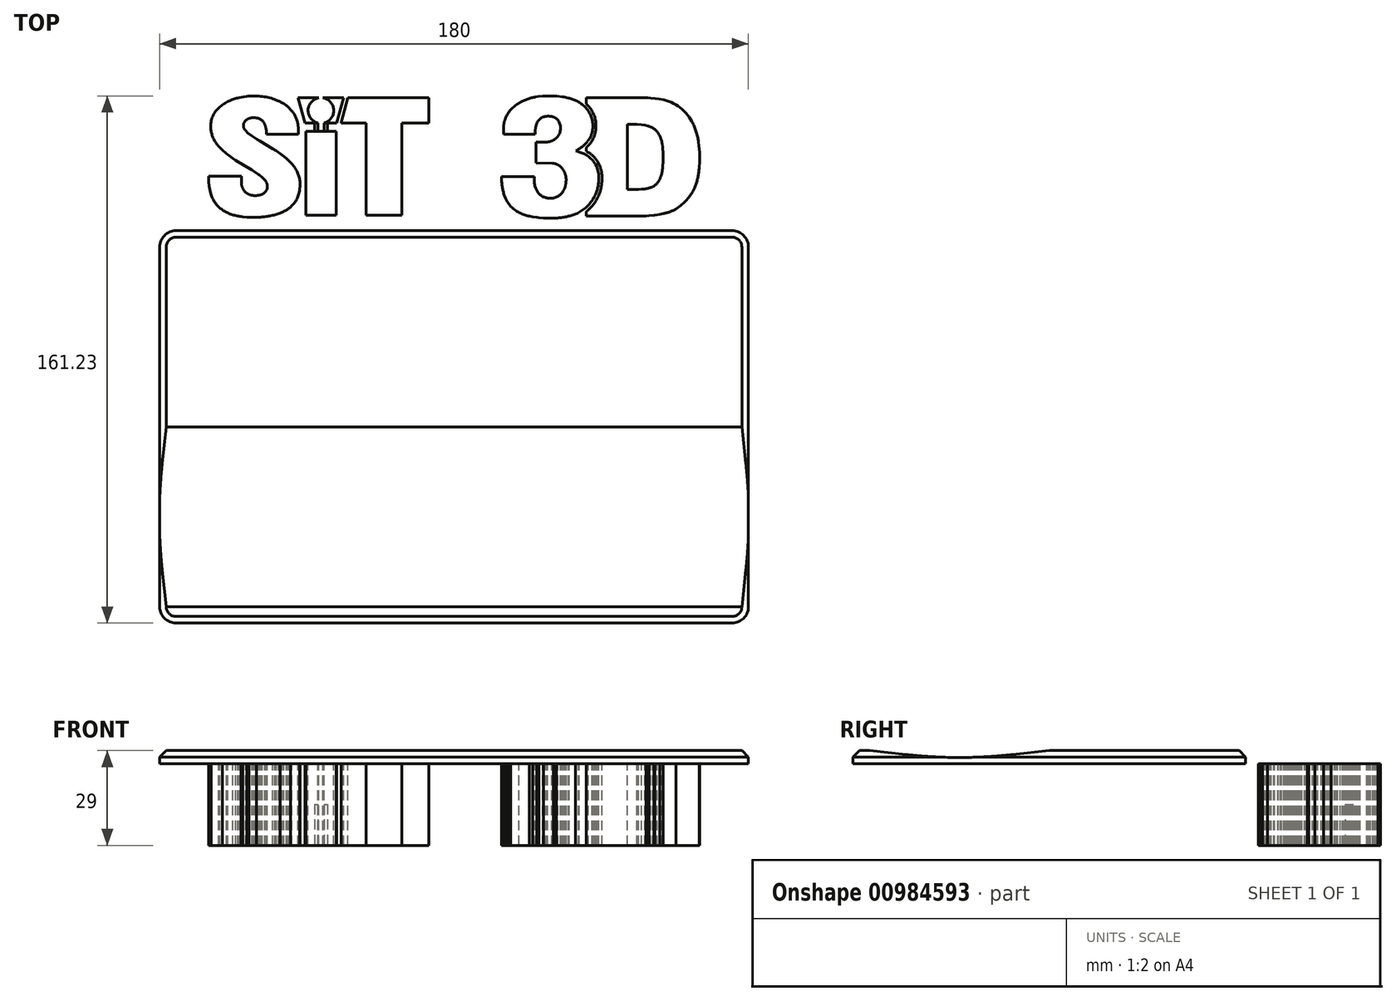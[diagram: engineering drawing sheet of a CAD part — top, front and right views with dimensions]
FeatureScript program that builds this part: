
annotation { "Feature Type Name" : "Feature", "Feature Type Description" : "" }
export const myFeature = defineFeature(function(context is Context, id is Id, definition is map)
    precondition{}
    {
        {
            var Q0;
            Q0=qCreatedBy(makeId("Top.planeOp"),FACE);
            var sketch = newSketch(context, id + "F0", { "sketchPlane" : qUnion([Q0])});
            skLineSegment(sketch, "E0", {"start": v(-41.68, 10.42) * mm, "end": v(-45.54, 10.42) * mm});
            skLineSegment(sketch, "E1", {"start": v(-45.54, 10.42) * mm, "end": v(-47.67, 18.07) * mm});
            skLineSegment(sketch, "E2", {"start": v(-47.67, 18.07) * mm, "end": v(-41.39, 18.07) * mm});
            skArc(sketch, "E3", {"start": v(-41.39, 18.07) * mm, "mid": v(-44.63, 14.36) * mm, "end": v(-41.68, 10.42) * mm});
            skLineSegment(sketch, "E4", {"start": v(-39.73, 10.42) * mm, "end": v(-35.87, 10.42) * mm});
            skLineSegment(sketch, "E5", {"start": v(-35.87, 10.42) * mm, "end": v(-33.73, 18.07) * mm});
            skLineSegment(sketch, "E6", {"start": v(-33.73, 18.07) * mm, "end": v(-40.04, 18.07) * mm});
            skArc(sketch, "E7", {"start": v(-40.04, 18.07) * mm, "mid": v(-36.8, 14.37) * mm, "end": v(-39.73, 10.42) * mm});
            skArc(sketch, "E8", {"start": v(62.12, 7.72) * mm, "mid": v(60.8, 8.85) * mm, "end": v(59.19, 9.54) * mm});
            skLineSegment(sketch, "E9", {"start": v(59.19, 9.54) * mm, "end": v(58.36, 9.75) * mm});
            skLineSegment(sketch, "E10", {"start": v(58.36, 9.75) * mm, "end": v(57.35, 9.9) * mm});
            skLineSegment(sketch, "E11", {"start": v(57.35, 9.9) * mm, "end": v(55.9, 9.97) * mm});
            skLineSegment(sketch, "E12", {"start": v(55.9, 9.97) * mm, "end": v(54.93, 9.97) * mm});
            skLineSegment(sketch, "E13", {"start": v(54.93, 9.97) * mm, "end": v(52.98, 9.95) * mm});
            skLineSegment(sketch, "E14", {"start": v(52.98, 9.95) * mm, "end": v(52.98, -9.88) * mm});
            skLineSegment(sketch, "E15", {"start": v(52.98, -9.88) * mm, "end": v(56.45, -9.88) * mm});
            skLineSegment(sketch, "E16", {"start": v(56.45, -9.88) * mm, "end": v(57.31, -9.84) * mm});
            skArc(sketch, "E17", {"start": v(57.31, -9.84) * mm, "mid": v(59.06, -9.64) * mm, "end": v(60.74, -9.12) * mm});
            skArc(sketch, "E18", {"start": v(60.74, -9.12) * mm, "mid": v(62, -8.1) * mm, "end": v(62.9, -6.77) * mm});
            skArc(sketch, "E19", {"start": v(62.9, -6.77) * mm, "mid": v(63.49, -5.13) * mm, "end": v(63.76, -3.41) * mm});
            skLineSegment(sketch, "E20", {"start": v(63.76, -3.41) * mm, "end": v(63.8, -3.09) * mm});
            skLineSegment(sketch, "E21", {"start": v(63.8, -3.09) * mm, "end": v(63.92, -1.2) * mm});
            skLineSegment(sketch, "E22", {"start": v(63.92, -1.2) * mm, "end": v(63.92, 0.88) * mm});
            skLineSegment(sketch, "E23", {"start": v(63.92, 0.88) * mm, "end": v(63.76, 2.98) * mm});
            skLineSegment(sketch, "E24", {"start": v(63.76, 2.98) * mm, "end": v(63.61, 4) * mm});
            skArc(sketch, "E25", {"start": v(63.61, 4) * mm, "mid": v(63.1, 5.95) * mm, "end": v(62.12, 7.72) * mm});
            skLineSegment(sketch, "E26", {"start": v(-36.04, -17.82) * mm, "end": v(-36.04, 7.85) * mm});
            skLineSegment(sketch, "E27", {"start": v(-36.04, 7.85) * mm, "end": v(-45.36, 7.85) * mm});
            skLineSegment(sketch, "E28", {"start": v(-45.36, 7.85) * mm, "end": v(-45.36, -17.82) * mm});
            skLineSegment(sketch, "E29", {"start": v(-45.36, -17.82) * mm, "end": v(-36.04, -17.82) * mm});
            skLineSegment(sketch, "E30", {"start": v(-16, -17.82) * mm, "end": v(-16, 10.42) * mm});
            skLineSegment(sketch, "E31", {"start": v(-16, 10.42) * mm, "end": v(-7.7, 10.42) * mm});
            skLineSegment(sketch, "E32", {"start": v(-7.7, 10.42) * mm, "end": v(-7.7, 18.07) * mm});
            skLineSegment(sketch, "E33", {"start": v(-7.7, 18.07) * mm, "end": v(-32.47, 18.07) * mm});
            skLineSegment(sketch, "E34", {"start": v(-32.47, 18.07) * mm, "end": v(-34.54, 10.53) * mm});
            skLineSegment(sketch, "E35", {"start": v(-34.54, 10.53) * mm, "end": v(-34.56, 10.42) * mm});
            skLineSegment(sketch, "E36", {"start": v(-34.56, 10.42) * mm, "end": v(-26.83, 10.42) * mm});
            skLineSegment(sketch, "E37", {"start": v(-26.83, 10.42) * mm, "end": v(-26.83, -17.82) * mm});
            skLineSegment(sketch, "E38", {"start": v(-26.83, -17.82) * mm, "end": v(-16, -17.82) * mm});
            skArc(sketch, "E39", {"start": v(72.72, 10.85) * mm, "mid": v(68.5, 15.56) * mm, "end": v(62.58, 17.8) * mm});
            skLineSegment(sketch, "E40", {"start": v(62.58, 17.8) * mm, "end": v(61.54, 17.95) * mm});
            skLineSegment(sketch, "E41", {"start": v(61.54, 17.95) * mm, "end": v(60.13, 18.06) * mm});
            skLineSegment(sketch, "E42", {"start": v(60.13, 18.06) * mm, "end": v(59.2, 18.1) * mm});
            skLineSegment(sketch, "E43", {"start": v(59.2, 18.1) * mm, "end": v(40.48, 18.11) * mm});
            skLineSegment(sketch, "E44", {"start": v(40.48, 18.11) * mm, "end": v(40.48, 16.27) * mm});
            skLineSegment(sketch, "E45", {"start": v(40.48, 16.27) * mm, "end": v(41.09, 15.61) * mm});
            skArc(sketch, "E46", {"start": v(41.09, 15.61) * mm, "mid": v(42.77, 12.88) * mm, "end": v(43.39, 9.73) * mm});
            skArc(sketch, "E47", {"start": v(43.39, 9.73) * mm, "mid": v(43.4, 9.14) * mm, "end": v(43.36, 8.54) * mm});
            skArc(sketch, "E48", {"start": v(43.36, 8.54) * mm, "mid": v(43.01, 6.8) * mm, "end": v(42.3, 5.18) * mm});
            skLineSegment(sketch, "E49", {"start": v(42.3, 5.18) * mm, "end": v(42.25, 5.11) * mm});
            skArc(sketch, "E50", {"start": v(42.25, 5.11) * mm, "mid": v(41.46, 3.94) * mm, "end": v(40.48, 2.9) * mm});
            skLineSegment(sketch, "E51", {"start": v(40.48, 2.9) * mm, "end": v(40.48, 1.75) * mm});
            skLineSegment(sketch, "E52", {"start": v(40.48, 1.75) * mm, "end": v(40.55, 1.7) * mm});
            skArc(sketch, "E53", {"start": v(40.55, 1.7) * mm, "mid": v(42.6, 0.21) * mm, "end": v(44.12, -1.83) * mm});
            skArc(sketch, "E54", {"start": v(44.12, -1.83) * mm, "mid": v(44.95, -3.96) * mm, "end": v(45.23, -6.23) * mm});
            skArc(sketch, "E55", {"start": v(45.23, -6.23) * mm, "mid": v(45.2, -7.76) * mm, "end": v(44.98, -9.27) * mm});
            skArc(sketch, "E56", {"start": v(44.98, -9.27) * mm, "mid": v(43.48, -13.18) * mm, "end": v(40.8, -16.4) * mm});
            skLineSegment(sketch, "E57", {"start": v(40.8, -16.4) * mm, "end": v(40.48, -16.67) * mm});
            skLineSegment(sketch, "E58", {"start": v(40.48, -16.67) * mm, "end": v(40.48, -18.04) * mm});
            skLineSegment(sketch, "E59", {"start": v(40.48, -18.04) * mm, "end": v(58.65, -18.04) * mm});
            skLineSegment(sketch, "E60", {"start": v(58.65, -18.04) * mm, "end": v(59.59, -17.99) * mm});
            skLineSegment(sketch, "E61", {"start": v(59.59, -17.99) * mm, "end": v(61.1, -17.84) * mm});
            skLineSegment(sketch, "E62", {"start": v(61.1, -17.84) * mm, "end": v(61.35, -17.8) * mm});
            skLineSegment(sketch, "E63", {"start": v(61.35, -17.8) * mm, "end": v(62.87, -17.56) * mm});
            skLineSegment(sketch, "E64", {"start": v(62.87, -17.56) * mm, "end": v(63.88, -17.34) * mm});
            skArc(sketch, "E65", {"start": v(63.88, -17.34) * mm, "mid": v(65.95, -16.77) * mm, "end": v(67.9, -15.84) * mm});
            skArc(sketch, "E66", {"start": v(67.9, -15.84) * mm, "mid": v(71.2, -13.05) * mm, "end": v(73.52, -9.4) * mm});
            skArc(sketch, "E67", {"start": v(73.52, -9.4) * mm, "mid": v(74.47, -6.58) * mm, "end": v(74.92, -3.63) * mm});
            skLineSegment(sketch, "E68", {"start": v(74.92, -3.63) * mm, "end": v(74.95, -3.27) * mm});
            skLineSegment(sketch, "E69", {"start": v(74.95, -3.27) * mm, "end": v(75.08, -1.35) * mm});
            skLineSegment(sketch, "E70", {"start": v(75.08, -1.35) * mm, "end": v(75.08, 1.32) * mm});
            skLineSegment(sketch, "E71", {"start": v(75.08, 1.32) * mm, "end": v(74.88, 3.56) * mm});
            skLineSegment(sketch, "E72", {"start": v(74.88, 3.56) * mm, "end": v(74.74, 4.6) * mm});
            skArc(sketch, "E73", {"start": v(74.74, 4.6) * mm, "mid": v(74, 7.81) * mm, "end": v(72.72, 10.85) * mm});
            skArc(sketch, "E74", {"start": v(-54.82, 17.63) * mm, "mid": v(-59.12, 18.57) * mm, "end": v(-63.53, 18.52) * mm});
            skLineSegment(sketch, "E75", {"start": v(-63.53, 18.52) * mm, "end": v(-64.32, 18.42) * mm});
            skLineSegment(sketch, "E76", {"start": v(-64.32, 18.42) * mm, "end": v(-65.7, 18.16) * mm});
            skLineSegment(sketch, "E77", {"start": v(-65.7, 18.16) * mm, "end": v(-66.13, 18.05) * mm});
            skArc(sketch, "E78", {"start": v(-66.13, 18.05) * mm, "mid": v(-69.19, 16.93) * mm, "end": v(-71.87, 15.08) * mm});
            skArc(sketch, "E79", {"start": v(-71.87, 15.08) * mm, "mid": v(-73.94, 12) * mm, "end": v(-74.38, 8.33) * mm});
            skArc(sketch, "E80", {"start": v(-74.38, 8.33) * mm, "mid": v(-73.54, 5.62) * mm, "end": v(-71.93, 3.28) * mm});
            skLineSegment(sketch, "E81", {"start": v(-71.93, 3.28) * mm, "end": v(-71.55, 2.86) * mm});
            skLineSegment(sketch, "E82", {"start": v(-71.55, 2.86) * mm, "end": v(-70.93, 2.22) * mm});
            skLineSegment(sketch, "E83", {"start": v(-70.93, 2.22) * mm, "end": v(-69.53, 1.02) * mm});
            skLineSegment(sketch, "E84", {"start": v(-69.53, 1.02) * mm, "end": v(-69.22, 0.79) * mm});
            skLineSegment(sketch, "E85", {"start": v(-69.22, 0.79) * mm, "end": v(-67.6, -0.4) * mm});
            skLineSegment(sketch, "E86", {"start": v(-67.6, -0.4) * mm, "end": v(-66.73, -0.98) * mm});
            skLineSegment(sketch, "E87", {"start": v(-66.73, -0.98) * mm, "end": v(-61.82, -4.02) * mm});
            skLineSegment(sketch, "E88", {"start": v(-61.82, -4.02) * mm, "end": v(-61.03, -4.52) * mm});
            skLineSegment(sketch, "E89", {"start": v(-61.03, -4.52) * mm, "end": v(-59.81, -5.34) * mm});
            skLineSegment(sketch, "E90", {"start": v(-59.81, -5.34) * mm, "end": v(-59.54, -5.53) * mm});
            skLineSegment(sketch, "E91", {"start": v(-59.54, -5.53) * mm, "end": v(-58.58, -6.3) * mm});
            skLineSegment(sketch, "E92", {"start": v(-58.58, -6.3) * mm, "end": v(-57.93, -6.95) * mm});
            skLineSegment(sketch, "E93", {"start": v(-57.93, -6.95) * mm, "end": v(-57.75, -7.18) * mm});
            skArc(sketch, "E94", {"start": v(-57.75, -7.18) * mm, "mid": v(-57.18, -9.72) * mm, "end": v(-59.05, -11.53) * mm});
            skArc(sketch, "E95", {"start": v(-59.05, -11.53) * mm, "mid": v(-60.3, -11.78) * mm, "end": v(-61.57, -11.74) * mm});
            skArc(sketch, "E96", {"start": v(-61.57, -11.74) * mm, "mid": v(-62.7, -11.44) * mm, "end": v(-63.68, -10.82) * mm});
            skArc(sketch, "E97", {"start": v(-63.68, -10.82) * mm, "mid": v(-64.62, -9.56) * mm, "end": v(-65.02, -8.04) * mm});
            skLineSegment(sketch, "E98", {"start": v(-65.02, -8.04) * mm, "end": v(-65.04, -5.9) * mm});
            skLineSegment(sketch, "E99", {"start": v(-65.04, -5.9) * mm, "end": v(-75.08, -5.9) * mm});
            skLineSegment(sketch, "E100", {"start": v(-75.08, -5.9) * mm, "end": v(-75.06, -6.88) * mm});
            skLineSegment(sketch, "E101", {"start": v(-75.06, -6.88) * mm, "end": v(-75.03, -7.53) * mm});
            skLineSegment(sketch, "E102", {"start": v(-75.03, -7.53) * mm, "end": v(-74.88, -8.94) * mm});
            skLineSegment(sketch, "E103", {"start": v(-74.88, -8.94) * mm, "end": v(-74.81, -9.4) * mm});
            skLineSegment(sketch, "E104", {"start": v(-74.81, -9.4) * mm, "end": v(-74.55, -10.64) * mm});
            skLineSegment(sketch, "E105", {"start": v(-74.55, -10.64) * mm, "end": v(-74.24, -11.64) * mm});
            skArc(sketch, "E106", {"start": v(-74.24, -11.64) * mm, "mid": v(-72.9, -14.16) * mm, "end": v(-70.85, -16.15) * mm});
            skArc(sketch, "E107", {"start": v(-70.85, -16.15) * mm, "mid": v(-68.12, -17.52) * mm, "end": v(-65.15, -18.2) * mm});
            skLineSegment(sketch, "E108", {"start": v(-65.15, -18.2) * mm, "end": v(-64.6, -18.27) * mm});
            skLineSegment(sketch, "E109", {"start": v(-64.6, -18.27) * mm, "end": v(-63.34, -18.38) * mm});
            skLineSegment(sketch, "E110", {"start": v(-63.34, -18.38) * mm, "end": v(-62.66, -18.42) * mm});
            skLineSegment(sketch, "E111", {"start": v(-62.66, -18.42) * mm, "end": v(-60.45, -18.44) * mm});
            skLineSegment(sketch, "E112", {"start": v(-60.45, -18.44) * mm, "end": v(-59.6, -18.4) * mm});
            skArc(sketch, "E113", {"start": v(-59.6, -18.4) * mm, "mid": v(-56.32, -18.02) * mm, "end": v(-53.13, -17.13) * mm});
            skArc(sketch, "E114", {"start": v(-53.13, -17.13) * mm, "mid": v(-51.52, -16.36) * mm, "end": v(-50.05, -15.34) * mm});
            skArc(sketch, "E115", {"start": v(-50.05, -15.34) * mm, "mid": v(-48, -12.7) * mm, "end": v(-47.15, -9.48) * mm});
            skArc(sketch, "E116", {"start": v(-47.15, -9.48) * mm, "mid": v(-47.08, -8.42) * mm, "end": v(-47.14, -7.35) * mm});
            skArc(sketch, "E117", {"start": v(-47.14, -7.35) * mm, "mid": v(-47.97, -4.52) * mm, "end": v(-49.63, -2.08) * mm});
            skLineSegment(sketch, "E118", {"start": v(-49.63, -2.08) * mm, "end": v(-49.9, -1.78) * mm});
            skLineSegment(sketch, "E119", {"start": v(-49.9, -1.78) * mm, "end": v(-50.88, -0.8) * mm});
            skLineSegment(sketch, "E120", {"start": v(-50.88, -0.8) * mm, "end": v(-51.25, -0.46) * mm});
            skLineSegment(sketch, "E121", {"start": v(-51.25, -0.46) * mm, "end": v(-52.47, 0.53) * mm});
            skLineSegment(sketch, "E122", {"start": v(-52.47, 0.53) * mm, "end": v(-52.88, 0.84) * mm});
            skLineSegment(sketch, "E123", {"start": v(-52.88, 0.84) * mm, "end": v(-54.32, 1.85) * mm});
            skLineSegment(sketch, "E124", {"start": v(-54.32, 1.85) * mm, "end": v(-55.44, 2.57) * mm});
            skLineSegment(sketch, "E125", {"start": v(-55.44, 2.57) * mm, "end": v(-59.45, 4.96) * mm});
            skLineSegment(sketch, "E126", {"start": v(-59.45, 4.96) * mm, "end": v(-60.24, 5.43) * mm});
            skLineSegment(sketch, "E127", {"start": v(-60.24, 5.43) * mm, "end": v(-61.83, 6.44) * mm});
            skLineSegment(sketch, "E128", {"start": v(-61.83, 6.44) * mm, "end": v(-63.05, 7.35) * mm});
            skLineSegment(sketch, "E129", {"start": v(-63.05, 7.35) * mm, "end": v(-63.78, 8.07) * mm});
            skArc(sketch, "E130", {"start": v(-63.78, 8.07) * mm, "mid": v(-64.37, 9.87) * mm, "end": v(-63.34, 11.47) * mm});
            skArc(sketch, "E131", {"start": v(-63.34, 11.47) * mm, "mid": v(-62.57, 11.84) * mm, "end": v(-61.72, 12.01) * mm});
            skArc(sketch, "E132", {"start": v(-61.72, 12.01) * mm, "mid": v(-61.1, 12.03) * mm, "end": v(-60.5, 11.96) * mm});
            skArc(sketch, "E133", {"start": v(-60.5, 11.96) * mm, "mid": v(-58.86, 11.3) * mm, "end": v(-57.83, 9.87) * mm});
            skArc(sketch, "E134", {"start": v(-57.83, 9.87) * mm, "mid": v(-57.44, 8.45) * mm, "end": v(-57.31, 6.99) * mm});
            skLineSegment(sketch, "E135", {"start": v(-57.31, 6.99) * mm, "end": v(-47.6, 6.99) * mm});
            skLineSegment(sketch, "E136", {"start": v(-47.6, 6.99) * mm, "end": v(-47.6, 8.87) * mm});
            skLineSegment(sketch, "E137", {"start": v(-47.6, 8.87) * mm, "end": v(-47.69, 9.7) * mm});
            skLineSegment(sketch, "E138", {"start": v(-47.69, 9.7) * mm, "end": v(-47.7, 9.73) * mm});
            skArc(sketch, "E139", {"start": v(-47.7, 9.73) * mm, "mid": v(-48.44, 12.3) * mm, "end": v(-49.94, 14.5) * mm});
            skLineSegment(sketch, "E140", {"start": v(-49.94, 14.5) * mm, "end": v(-50.56, 15.15) * mm});
            skLineSegment(sketch, "E141", {"start": v(-50.56, 15.15) * mm, "end": v(-51.07, 15.57) * mm});
            skLineSegment(sketch, "E142", {"start": v(-51.07, 15.57) * mm, "end": v(-51.25, 15.72) * mm});
            skLineSegment(sketch, "E143", {"start": v(-51.25, 15.72) * mm, "end": v(-52.08, 16.3) * mm});
            skLineSegment(sketch, "E144", {"start": v(-52.08, 16.3) * mm, "end": v(-52.48, 16.55) * mm});
            skLineSegment(sketch, "E145", {"start": v(-52.48, 16.55) * mm, "end": v(-53.52, 17.1) * mm});
            skLineSegment(sketch, "E146", {"start": v(-53.52, 17.1) * mm, "end": v(-53.63, 17.14) * mm});
            skLineSegment(sketch, "E147", {"start": v(-53.63, 17.14) * mm, "end": v(-54.64, 17.56) * mm});
            skLineSegment(sketch, "E148", {"start": v(-54.64, 17.56) * mm, "end": v(-54.82, 17.63) * mm});
            skArc(sketch, "E149", {"start": v(19.83, 16.49) * mm, "mid": v(17.46, 14.6) * mm, "end": v(15.8, 12.05) * mm});
            skArc(sketch, "E150", {"start": v(15.8, 12.05) * mm, "mid": v(15.33, 10.61) * mm, "end": v(15.1, 9.12) * mm});
            skLineSegment(sketch, "E151", {"start": v(15.1, 9.12) * mm, "end": v(15.1, 7.02) * mm});
            skLineSegment(sketch, "E152", {"start": v(15.1, 7.02) * mm, "end": v(24.81, 7.02) * mm});
            skArc(sketch, "E153", {"start": v(24.81, 7.02) * mm, "mid": v(24.92, 8.9) * mm, "end": v(25.47, 10.7) * mm});
            skArc(sketch, "E154", {"start": v(25.47, 10.7) * mm, "mid": v(26.47, 11.8) * mm, "end": v(27.84, 12.38) * mm});
            skArc(sketch, "E155", {"start": v(27.84, 12.38) * mm, "mid": v(29.13, 12.48) * mm, "end": v(30.4, 12.25) * mm});
            skArc(sketch, "E156", {"start": v(30.4, 12.25) * mm, "mid": v(31.17, 11.84) * mm, "end": v(31.82, 11.25) * mm});
            skArc(sketch, "E157", {"start": v(31.82, 11.25) * mm, "mid": v(32.55, 8.3) * mm, "end": v(31.1, 5.65) * mm});
            skLineSegment(sketch, "E158", {"start": v(31.1, 5.65) * mm, "end": v(31.02, 5.62) * mm});
            skArc(sketch, "E159", {"start": v(31.02, 5.62) * mm, "mid": v(29.8, 4.89) * mm, "end": v(28.42, 4.59) * mm});
            skLineSegment(sketch, "E160", {"start": v(28.42, 4.59) * mm, "end": v(25.03, 4.57) * mm});
            skLineSegment(sketch, "E161", {"start": v(25.03, 4.57) * mm, "end": v(25.03, -1.86) * mm});
            skLineSegment(sketch, "E162", {"start": v(25.03, -1.86) * mm, "end": v(30.05, -1.88) * mm});
            skLineSegment(sketch, "E163", {"start": v(30.05, -1.88) * mm, "end": v(30.3, -1.91) * mm});
            skArc(sketch, "E164", {"start": v(30.3, -1.91) * mm, "mid": v(31.51, -2.26) * mm, "end": v(32.58, -2.93) * mm});
            skLineSegment(sketch, "E165", {"start": v(32.58, -2.93) * mm, "end": v(32.98, -3.33) * mm});
            skArc(sketch, "E166", {"start": v(32.98, -3.33) * mm, "mid": v(33.85, -4.81) * mm, "end": v(34.27, -6.48) * mm});
            skArc(sketch, "E167", {"start": v(34.27, -6.48) * mm, "mid": v(34.15, -8.23) * mm, "end": v(33.67, -9.92) * mm});
            skLineSegment(sketch, "E168", {"start": v(33.67, -9.92) * mm, "end": v(33.37, -10.5) * mm});
            skArc(sketch, "E169", {"start": v(33.37, -10.5) * mm, "mid": v(31.32, -12.25) * mm, "end": v(28.64, -12.56) * mm});
            skArc(sketch, "E170", {"start": v(28.64, -12.56) * mm, "mid": v(26.55, -11.73) * mm, "end": v(25.13, -9.99) * mm});
            skLineSegment(sketch, "E171", {"start": v(25.13, -9.99) * mm, "end": v(24.9, -9.45) * mm});
            skLineSegment(sketch, "E172", {"start": v(24.9, -9.45) * mm, "end": v(24.72, -8.83) * mm});
            skLineSegment(sketch, "E173", {"start": v(24.72, -8.83) * mm, "end": v(24.65, -8.5) * mm});
            skLineSegment(sketch, "E174", {"start": v(24.65, -8.5) * mm, "end": v(24.6, -7.88) * mm});
            skLineSegment(sketch, "E175", {"start": v(24.6, -7.88) * mm, "end": v(24.6, -6.05) * mm});
            skLineSegment(sketch, "E176", {"start": v(24.6, -6.05) * mm, "end": v(14.55, -6.05) * mm});
            skArc(sketch, "E177", {"start": v(14.55, -6.05) * mm, "mid": v(14.72, -9.01) * mm, "end": v(15.43, -11.9) * mm});
            skLineSegment(sketch, "E178", {"start": v(15.43, -11.9) * mm, "end": v(15.74, -12.66) * mm});
            skLineSegment(sketch, "E179", {"start": v(15.74, -12.66) * mm, "end": v(16.3, -13.7) * mm});
            skLineSegment(sketch, "E180", {"start": v(16.3, -13.7) * mm, "end": v(16.42, -13.9) * mm});
            skLineSegment(sketch, "E181", {"start": v(16.42, -13.9) * mm, "end": v(17.04, -14.72) * mm});
            skLineSegment(sketch, "E182", {"start": v(17.04, -14.72) * mm, "end": v(17.33, -15.08) * mm});
            skArc(sketch, "E183", {"start": v(17.33, -15.08) * mm, "mid": v(19.98, -17.01) * mm, "end": v(23.08, -18.1) * mm});
            skLineSegment(sketch, "E184", {"start": v(23.08, -18.1) * mm, "end": v(24.09, -18.3) * mm});
            skLineSegment(sketch, "E185", {"start": v(24.09, -18.3) * mm, "end": v(25.25, -18.5) * mm});
            skLineSegment(sketch, "E186", {"start": v(25.25, -18.5) * mm, "end": v(25.93, -18.56) * mm});
            skLineSegment(sketch, "E187", {"start": v(25.93, -18.56) * mm, "end": v(27.34, -18.64) * mm});
            skLineSegment(sketch, "E188", {"start": v(27.34, -18.64) * mm, "end": v(30.34, -18.69) * mm});
            skLineSegment(sketch, "E189", {"start": v(30.34, -18.69) * mm, "end": v(31.3, -18.68) * mm});
            skArc(sketch, "E190", {"start": v(31.3, -18.68) * mm, "mid": v(34.29, -18.3) * mm, "end": v(37.16, -17.43) * mm});
            skArc(sketch, "E191", {"start": v(37.16, -17.43) * mm, "mid": v(40.3, -15.49) * mm, "end": v(42.64, -12.62) * mm});
            skLineSegment(sketch, "E192", {"start": v(42.64, -12.62) * mm, "end": v(42.69, -12.55) * mm});
            skArc(sketch, "E193", {"start": v(42.69, -12.55) * mm, "mid": v(43.8, -9.9) * mm, "end": v(44.26, -7.06) * mm});
            skArc(sketch, "E194", {"start": v(44.26, -7.06) * mm, "mid": v(44.17, -5.1) * mm, "end": v(43.67, -3.2) * mm});
            skLineSegment(sketch, "E195", {"start": v(43.67, -3.2) * mm, "end": v(43.54, -2.87) * mm});
            skLineSegment(sketch, "E196", {"start": v(43.54, -2.87) * mm, "end": v(43.18, -2.19) * mm});
            skLineSegment(sketch, "E197", {"start": v(43.18, -2.19) * mm, "end": v(43.08, -1.97) * mm});
            skArc(sketch, "E198", {"start": v(43.08, -1.97) * mm, "mid": v(41.02, 0.22) * mm, "end": v(38.31, 1.52) * mm});
            skLineSegment(sketch, "E199", {"start": v(38.31, 1.52) * mm, "end": v(37.95, 1.63) * mm});
            skLineSegment(sketch, "E200", {"start": v(37.95, 1.63) * mm, "end": v(37.27, 1.82) * mm});
            skLineSegment(sketch, "E201", {"start": v(37.27, 1.82) * mm, "end": v(37.27, 1.9) * mm});
            skArc(sketch, "E202", {"start": v(37.27, 1.9) * mm, "mid": v(39.24, 3.2) * mm, "end": v(40.9, 4.86) * mm});
            skLineSegment(sketch, "E203", {"start": v(40.9, 4.86) * mm, "end": v(40.95, 4.93) * mm});
            skArc(sketch, "E204", {"start": v(40.95, 4.93) * mm, "mid": v(41.99, 6.86) * mm, "end": v(42.41, 9) * mm});
            skArc(sketch, "E205", {"start": v(42.41, 9) * mm, "mid": v(41.96, 12.25) * mm, "end": v(40.28, 15.05) * mm});
            skArc(sketch, "E206", {"start": v(40.28, 15.05) * mm, "mid": v(37.96, 16.9) * mm, "end": v(35.2, 18) * mm});
            skLineSegment(sketch, "E207", {"start": v(35.2, 18) * mm, "end": v(35, 18.05) * mm});
            skLineSegment(sketch, "E208", {"start": v(35, 18.05) * mm, "end": v(33.55, 18.35) * mm});
            skLineSegment(sketch, "E209", {"start": v(33.55, 18.35) * mm, "end": v(33.12, 18.41) * mm});
            skLineSegment(sketch, "E210", {"start": v(33.12, 18.41) * mm, "end": v(31.42, 18.6) * mm});
            skLineSegment(sketch, "E211", {"start": v(31.42, 18.6) * mm, "end": v(30.84, 18.63) * mm});
            skLineSegment(sketch, "E212", {"start": v(30.84, 18.63) * mm, "end": v(29.9, 18.69) * mm});
            skLineSegment(sketch, "E213", {"start": v(29.9, 18.69) * mm, "end": v(28.28, 18.69) * mm});
            skLineSegment(sketch, "E214", {"start": v(28.28, 18.69) * mm, "end": v(27.05, 18.64) * mm});
            skLineSegment(sketch, "E215", {"start": v(27.05, 18.64) * mm, "end": v(25.72, 18.5) * mm});
            skLineSegment(sketch, "E216", {"start": v(25.72, 18.5) * mm, "end": v(24.99, 18.38) * mm});
            skArc(sketch, "E217", {"start": v(24.99, 18.38) * mm, "mid": v(22.32, 17.68) * mm, "end": v(19.83, 16.49) * mm});
            skArc(sketch, "E218", {"start": v(15.4, 13.41) * mm, "mid": v(16.49, 14.95) * mm, "end": v(17.84, 16.27) * mm});
            skLineSegment(sketch, "E219", {"start": v(17.84, 16.27) * mm, "end": v(18.36, 16.72) * mm});
            skLineSegment(sketch, "E220", {"start": v(18.36, 16.72) * mm, "end": v(18.63, 18.07) * mm});
            skLineSegment(sketch, "E221", {"start": v(18.63, 18.07) * mm, "end": v(-6.54, 18.07) * mm});
            skLineSegment(sketch, "E222", {"start": v(-6.54, 18.07) * mm, "end": v(-6.54, -17.86) * mm});
            skLineSegment(sketch, "E223", {"start": v(-6.54, -17.86) * mm, "end": v(17.48, -17.86) * mm});
            skLineSegment(sketch, "E224", {"start": v(17.48, -17.86) * mm, "end": v(17.48, -16.52) * mm});
            skLineSegment(sketch, "E225", {"start": v(17.48, -16.52) * mm, "end": v(16.31, -15.37) * mm});
            skLineSegment(sketch, "E226", {"start": v(16.31, -15.37) * mm, "end": v(16.15, -15.18) * mm});
            skArc(sketch, "E227", {"start": v(16.15, -15.18) * mm, "mid": v(14.74, -12.83) * mm, "end": v(13.94, -10.2) * mm});
            skLineSegment(sketch, "E228", {"start": v(13.94, -10.2) * mm, "end": v(4.23, -10.17) * mm});
            skLineSegment(sketch, "E229", {"start": v(4.23, -10.17) * mm, "end": v(4.23, -3.12) * mm});
            skLineSegment(sketch, "E230", {"start": v(4.23, -3.12) * mm, "end": v(14.7, -3.12) * mm});
            skLineSegment(sketch, "E231", {"start": v(14.7, -3.12) * mm, "end": v(14.7, 4.5) * mm});
            skLineSegment(sketch, "E232", {"start": v(14.7, 4.5) * mm, "end": v(4.23, 4.5) * mm});
            skLineSegment(sketch, "E233", {"start": v(4.23, 4.5) * mm, "end": v(4.23, 10.6) * mm});
            skLineSegment(sketch, "E234", {"start": v(4.23, 10.6) * mm, "end": v(14.34, 10.64) * mm});
            skArc(sketch, "E235", {"start": v(14.34, 10.64) * mm, "mid": v(14.76, 12.06) * mm, "end": v(15.4, 13.41) * mm});
            skSolve(sketch);
        }
        {
            var Q0;
            Q0=makeQuery(id+"F0.imprint","IMPRINT",FACE,{"disambiguationData":[TD([[makeQuery(id+"F0.imprint","IMPRINT",EDGE,{"derivedFrom":sQuery(id+"F0.wireOp",EDGE,"E0")}),-1.0]])]});
            var Q1;
            Q1=makeQuery(id+"F0.imprint","IMPRINT",FACE,{"disambiguationData":[TD([[makeQuery(id+"F0.imprint","IMPRINT",EDGE,{"derivedFrom":sQuery(id+"F0.wireOp",EDGE,"E218")}),1.0]])]});
            var Q2;
            Q2=makeQuery(id+"F0.imprint","IMPRINT",FACE,{"disambiguationData":[TD([[makeQuery(id+"F0.imprint","IMPRINT",EDGE,{"derivedFrom":sQuery(id+"F0.wireOp",EDGE,"E30")}),1.0]])]});
            var Q3;
            Q3=makeQuery(id+"F0.imprint","IMPRINT",FACE,{"disambiguationData":[TD([[makeQuery(id+"F0.imprint","IMPRINT",EDGE,{"derivedFrom":sQuery(id+"F0.wireOp",EDGE,"E4")}),1.0]])]});
            var Q4;
            Q4=makeQuery(id+"F0.imprint","IMPRINT",FACE,{"disambiguationData":[TD([[makeQuery(id+"F0.imprint","IMPRINT",EDGE,{"derivedFrom":sQuery(id+"F0.wireOp",EDGE,"E26")}),1.0]])]});
            var Q5;
            Q5=makeQuery(id+"F0.imprint","IMPRINT",FACE,{"disambiguationData":[TD([[makeQuery(id+"F0.imprint","IMPRINT",EDGE,{"derivedFrom":sQuery(id+"F0.wireOp",EDGE,"E74")}),1.0]])]});
            extrude(context, id + "F1", {"entities" : qUnion([Q0, Q1, Q2, Q3, Q4, Q5]), "oppositeDirection" : true, "depth" : 25 * mm, "offsetDistance" : 25 * mm});
        }
        {
            var Q0;
            Q0=makeQuery(id+"F0.imprint","IMPRINT",FACE,{"disambiguationData":[TD([[makeQuery(id+"F0.imprint","IMPRINT",EDGE,{"derivedFrom":sQuery(id+"F0.wireOp",EDGE,"E149")}),1.0]])]});
            var Q1;
            Q1=makeQuery(id+"F0.imprint","IMPRINT",FACE,{"disambiguationData":[TD([[makeQuery(id+"F0.imprint","IMPRINT",EDGE,{"derivedFrom":sQuery(id+"F0.wireOp",EDGE,"E8")}),-1.0]])]});
            extrude(context, id + "F2", {"entities" : qUnion([Q0, Q1]), "oppositeDirection" : true, "depth" : 25 * mm, "offsetDistance" : 25 * mm});
        }
        {
            var Q0;
            Q0=makeQuery(id+"F1.opExtrude","SWEPT_FACE",FACE,{"disambiguationData":[OSD([sQuery(id+"F0.wireOp",EDGE,"E0")])]});
            var sketch = newSketch(context, id + "F3", { "sketchPlane" : qUnion([Q0])});
            skLineSegment(sketch, "E236.0", {"start": v(-42.68, -25) * mm, "end": v(-42.68, 0) * mm});
            skLineSegment(sketch, "E237", {"start": v(-42.68, 0) * mm, "end": v(-41.68, 0) * mm});
            skLineSegment(sketch, "E238", {"start": v(-41.68, 0) * mm, "end": v(-41.68, -25) * mm});
            skLineSegment(sketch, "E239", {"start": v(-41.68, -25) * mm, "end": v(-42.68, -25) * mm});
            skLineSegment(sketch, "E240", {"start": v(-41.68, -12.5) * mm, "end": v(-42.68, -12.5) * mm});
            skSolve(sketch);
        }
        {
            var Q0;
            Q0=makeQuery(id+"F1.opExtrude","SWEPT_FACE",FACE,{"disambiguationData":[OSD([sQuery(id+"F0.wireOp",EDGE,"E4")])]});
            var sketch = newSketch(context, id + "F4", { "sketchPlane" : qUnion([Q0])});
            skLineSegment(sketch, "E241.0", {"start": v(-38.73, -25) * mm, "end": v(-38.73, 0) * mm});
            skLineSegment(sketch, "E242", {"start": v(-38.73, 0) * mm, "end": v(-39.73, 0) * mm});
            skLineSegment(sketch, "E243", {"start": v(-39.73, 0) * mm, "end": v(-39.73, -25) * mm});
            skLineSegment(sketch, "E244", {"start": v(-39.73, -25) * mm, "end": v(-38.73, -25) * mm});
            skLineSegment(sketch, "E245", {"start": v(-38.73, -12.5) * mm, "end": v(-39.73, -12.5) * mm});
            skSolve(sketch);
        }
        {
            var Q0;
            {var subQ0=sQuery(id+"F4.wireOp",EDGE,"E244");Q0=makeQuery(id+"F4.imprint","IMPRINT",FACE,{"disambiguationData":[TD([[makeQuery(id+"F4.imprint","IMPRINT",EDGE,{"derivedFrom":subQ0}),1.0]])]});}
            var Q1;
            {var subQ0=sQuery(id+"F3.wireOp",EDGE,"E239");Q1=makeQuery(id+"F3.imprint","IMPRINT",FACE,{"disambiguationData":[TD([[makeQuery(id+"F3.imprint","IMPRINT",EDGE,{"derivedFrom":subQ0}),-1.0]])]});}
            extrude(context, id + "F5", {"entities" : qUnion([Q0, Q1]), "endBound" : BoundingType.UP_TO_NEXT, "depth" : 25 * mm, "offsetDistance" : 25 * mm});
        }
        {
            var Q0;
            Q0=qCreatedBy(makeId("Top.planeOp"),FACE);
            var sketch = newSketch(context, id + "F6", { "sketchPlane" : qUnion([Q0])});
            skLineSegment(sketch, "E246.bottom", {"start": v(-85, -22.54) * mm, "end": v(85, -22.54) * mm});
            skLineSegment(sketch, "E246.top", {"start": v(-85, -142.54) * mm, "end": v(85, -142.54) * mm});
            skLineSegment(sketch, "E246.left", {"start": v(-90, -27.54) * mm, "end": v(-90, -137.54) * mm});
            skLineSegment(sketch, "E246.right", {"start": v(90, -27.54) * mm, "end": v(90, -137.54) * mm});
            skPoint(sketch, "E247.visualSharp", {"position": v(-90, -22.54) * mm});
            skArc(sketch, "E247.filletArc", {"start": v(-85, -22.54) * mm, "mid": v(-88.54, -24) * mm, "end": v(-90, -27.54) * mm});
            skPoint(sketch, "E248.visualSharp", {"position": v(-88, -24.54) * mm});
            skPoint(sketch, "E249.visualSharp", {"position": v(-88, -140.54) * mm});
            skPoint(sketch, "E250.visualSharp", {"position": v(88, -140.54) * mm});
            skPoint(sketch, "E251.visualSharp", {"position": v(88, -24.54) * mm});
            skPoint(sketch, "E252.visualSharp", {"position": v(-90, -142.54) * mm});
            skArc(sketch, "E252.filletArc", {"start": v(-90, -137.54) * mm, "mid": v(-88.54, -141.07) * mm, "end": v(-85, -142.54) * mm});
            skArc(sketch, "E253.filletArc", {"start": v(85, -142.54) * mm, "mid": v(88.54, -141.07) * mm, "end": v(90, -137.54) * mm});
            skPoint(sketch, "E254.visualSharp", {"position": v(90, -22.54) * mm});
            skArc(sketch, "E254.filletArc", {"start": v(90, -27.54) * mm, "mid": v(88.54, -24) * mm, "end": v(85, -22.54) * mm});
            skSolve(sketch);
        }
        {
            var Q0;
            Q0 = qSketchRegion(id + "F6", true);
            extrude(context, id + "F7", {"entities" : qUnion([Q0]), "depth" : 4 * mm, "offsetDistance" : 25 * mm});
        }
        {
            var Q0;
            Q0=makeQuery(id+"F7.opExtrude","SWEPT_FACE",FACE,{"disambiguationData":[OSD([sQuery(id+"F6.wireOp",EDGE,"E246.left")])]});
            var sketch = newSketch(context, id + "F8", { "sketchPlane" : qUnion([Q0])});
            skPoint(sketch, "E255.orphan", {"position": v(27.54, 1) * mm});
            skLineSegment(sketch, "E256", {"start": v(82.54, 4) * mm, "end": v(93.77, 2.77) * mm});
            skLineSegment(sketch, "E257", {"start": v(126.3, 2.77) * mm, "end": v(137.54, 4) * mm});
            skPoint(sketch, "E258.visualSharp", {"position": v(110.04, 1) * mm});
            skArc(sketch, "E258.filletArc", {"start": v(93.77, 2.77) * mm, "mid": v(110.04, 1.89) * mm, "end": v(126.3, 2.77) * mm});
            skSolve(sketch);
        }
        {
            var Q0;
            {var subQ0=sQuery(id+"F8.wireOp",EDGE,"E256");Q0=makeQuery(id+"F8.imprint","IMPRINT",FACE,{"disambiguationData":[TD([[makeQuery(id+"F8.imprint","IMPRINT",EDGE,{"derivedFrom":subQ0}),1.0]])]});}
            extrude(context, id + "F9", {"entities" : qUnion([Q0]), "operationType" : NewBodyOperationType.REMOVE, "endBound" : BoundingType.THROUGH_ALL, "oppositeDirection" : true, "depth" : 25 * mm, "offsetDistance" : 25 * mm});
        }
        {
            var Q0;
            Q0=makeQuery(id+"F7.opExtrude","CAP_EDGE",EDGE,{"disambiguationData":[OSD([sQuery(id+"F6.wireOp",EDGE,"E246.left")])],"isStart":false});
            var Q1;
            Q1=makeQuery(id+"F7.opExtrude","CAP_EDGE",EDGE,{"disambiguationData":[OSD([sQuery(id+"F6.wireOp",EDGE,"E246.top")])],"isStart":false});
            chamfer(context, id + "F10", {"entities" : qUnion([Q0, Q1]), "width" : 2 * mm, "tangentPropagation" : true});
        }
    });
